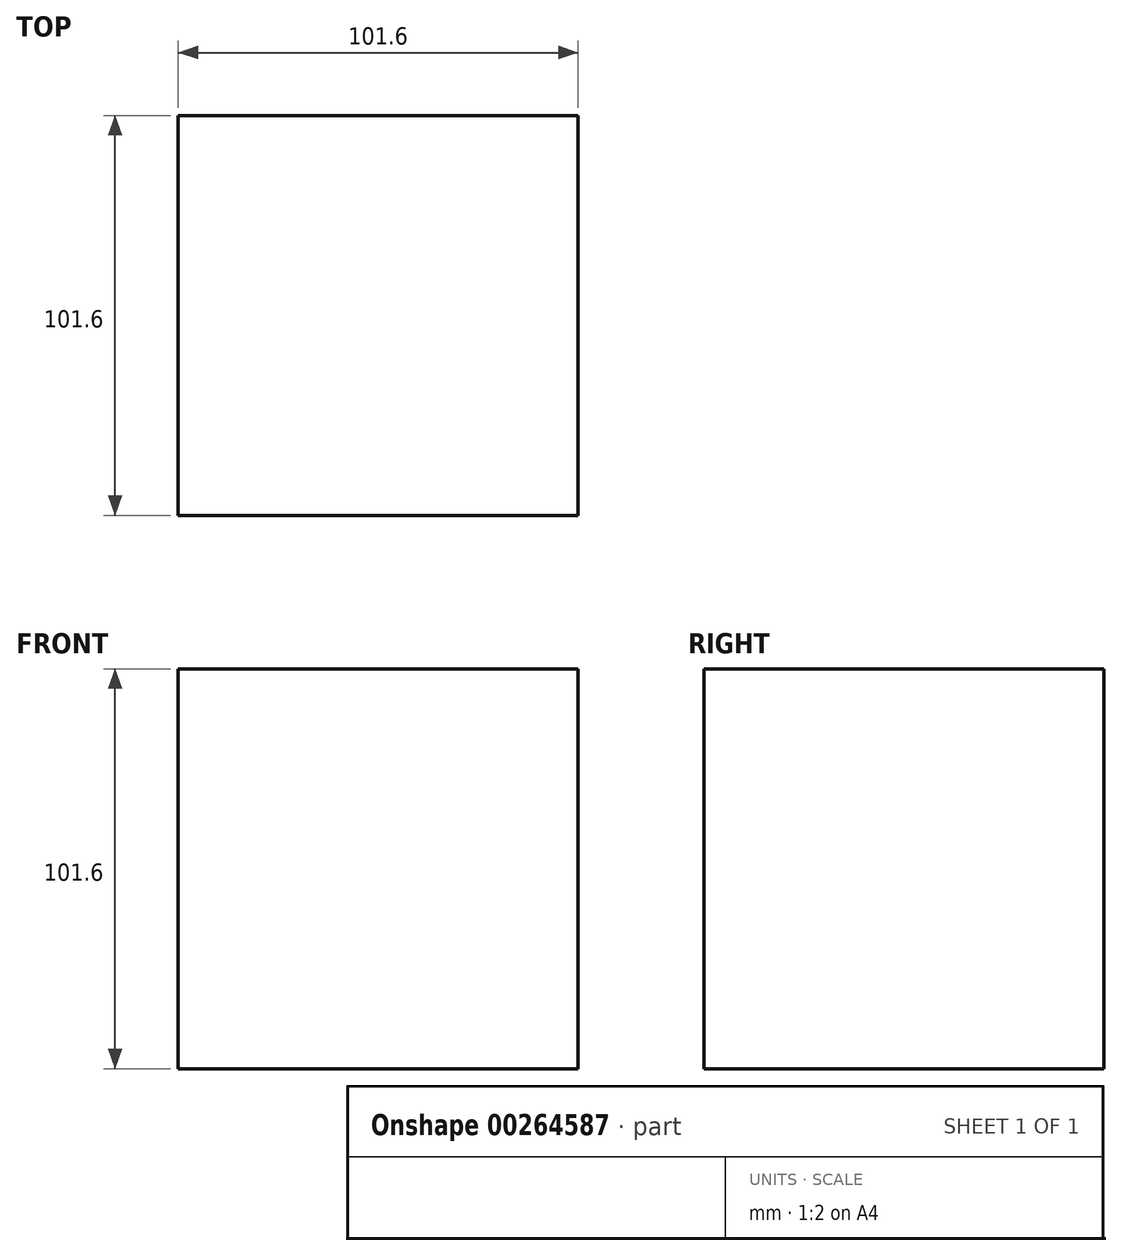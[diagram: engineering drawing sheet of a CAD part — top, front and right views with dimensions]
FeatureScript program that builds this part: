
annotation { "Feature Type Name" : "Feature", "Feature Type Description" : "" }
export const myFeature = defineFeature(function(context is Context, id is Id, definition is map)
    precondition{}
    {
        {
            var Q0;
            Q0=qCreatedBy(makeId("Front.planeOp"),FACE);
            var sketch = newSketch(context, id + "F0", { "sketchPlane" : qUnion([Q0])});
            skLineSegment(sketch, "E0.bottom", {"start": v(0, 0) * mm, "end": v(-101.6, 0) * mm});
            skLineSegment(sketch, "E0.top", {"start": v(0, 101.6) * mm, "end": v(-101.6, 101.6) * mm});
            skLineSegment(sketch, "E0.left", {"start": v(0, 0) * mm, "end": v(0, 101.6) * mm});
            skLineSegment(sketch, "E0.right", {"start": v(-101.6, 0) * mm, "end": v(-101.6, 101.6) * mm});
            skSolve(sketch);
        }
        {
            var Q0;
            Q0 = qSketchRegion(id + "F0", true);
            extrude(context, id + "F1", {"entities" : qUnion([Q0]), "depth" : 101.6 * mm});
        }
    });
